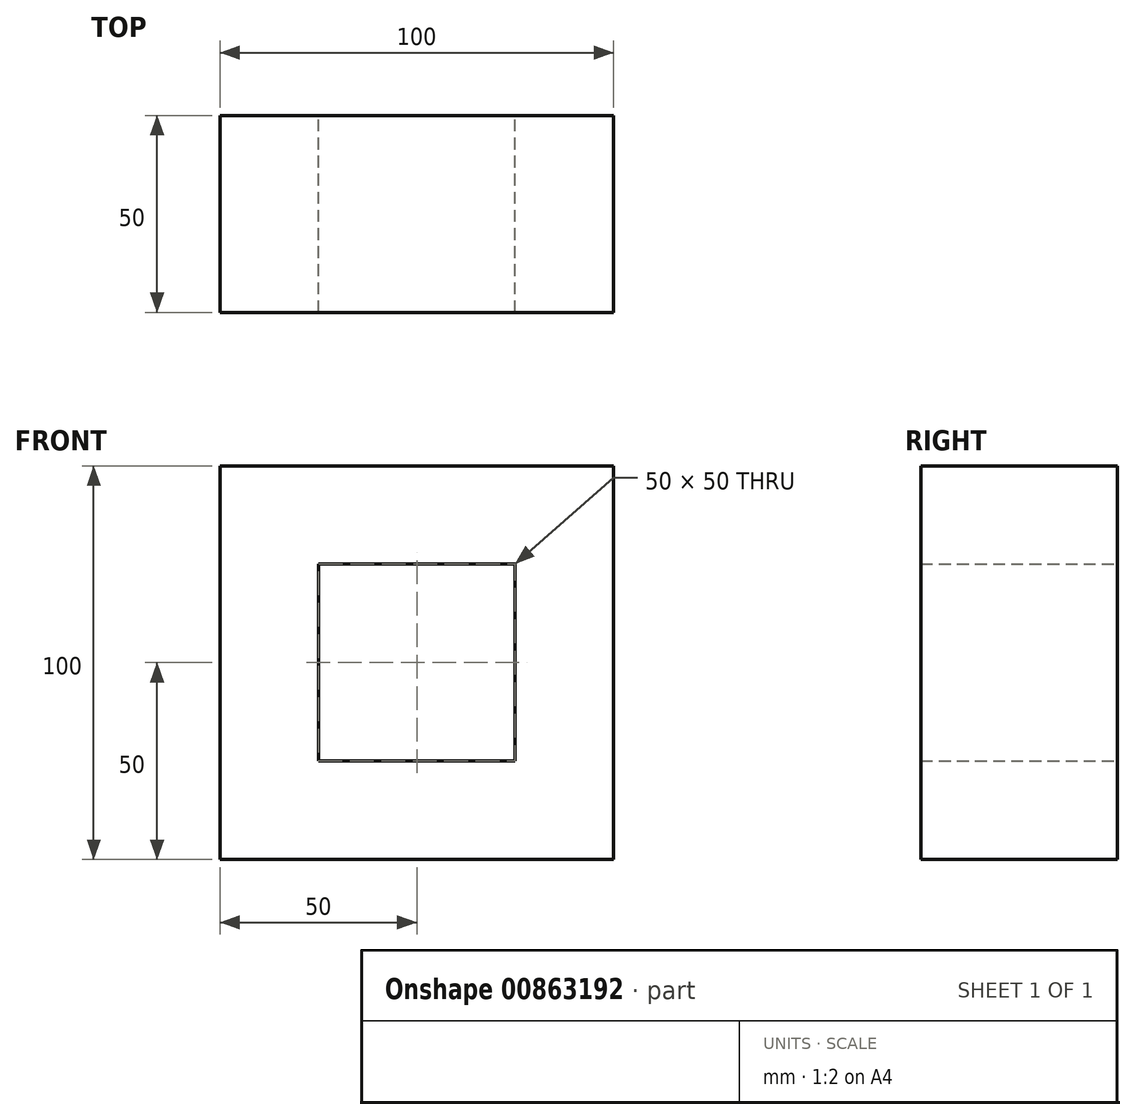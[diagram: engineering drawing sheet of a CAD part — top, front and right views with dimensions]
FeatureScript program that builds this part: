
annotation { "Feature Type Name" : "Feature", "Feature Type Description" : "" }
export const myFeature = defineFeature(function(context is Context, id is Id, definition is map)
    precondition{}
    {
        {
            var Q0;
            Q0=qCreatedBy(makeId("Front.planeOp"),FACE);
            var sketch = newSketch(context, id + "F0", { "sketchPlane" : qUnion([Q0])});
            skLineSegment(sketch, "E0.bottom", {"start": v(0, 0) * mm, "end": v(100, 0) * mm});
            skLineSegment(sketch, "E0.top", {"start": v(0, 100) * mm, "end": v(100, 100) * mm});
            skLineSegment(sketch, "E0.left", {"start": v(0, 0) * mm, "end": v(0, 100) * mm});
            skLineSegment(sketch, "E0.right", {"start": v(100, 0) * mm, "end": v(100, 100) * mm});
            skLineSegment(sketch, "E1", {"start": v(25, 75) * mm, "end": v(75, 75) * mm});
            skLineSegment(sketch, "E2", {"start": v(75, 75) * mm, "end": v(75, 25) * mm});
            skLineSegment(sketch, "E3", {"start": v(75, 25) * mm, "end": v(25, 25) * mm});
            skLineSegment(sketch, "E4", {"start": v(25, 25) * mm, "end": v(25, 75) * mm});
            skSolve(sketch);
        }
        {
            var Q0;
            Q0 = qSketchRegion(id + "F0", true);
            extrude(context, id + "F1", {"entities" : qUnion([Q0]), "depth" : 50 * mm, "offsetDistance" : 25 * mm});
        }
    });
